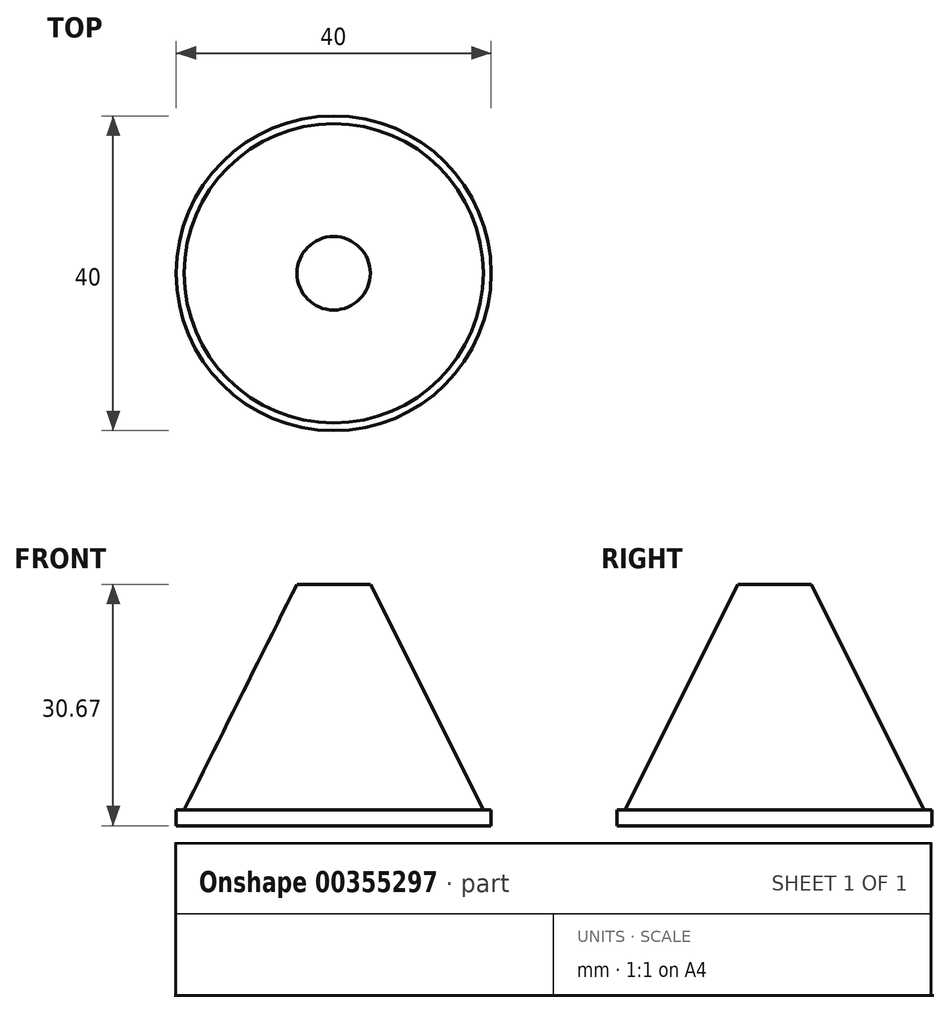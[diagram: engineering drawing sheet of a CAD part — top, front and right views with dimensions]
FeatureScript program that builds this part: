
annotation { "Feature Type Name" : "Feature", "Feature Type Description" : "" }
export const myFeature = defineFeature(function(context is Context, id is Id, definition is map)
    precondition{}
    {
        {
            var Q0;
            Q0=qCreatedBy(makeId("Front.planeOp"),FACE);
            var sketch = newSketch(context, id + "F0", { "sketchPlane" : qUnion([Q0])});
            skLineSegment(sketch, "E0", {"start": v(0, 0) * mm, "end": v(0, 40) * mm});
            skLineSegment(sketch, "E1", {"start": v(0, 40) * mm, "end": v(20, 0) * mm});
            skLineSegment(sketch, "E2", {"start": v(20, 0) * mm, "end": v(0, 0) * mm});
            skSolve(sketch);
        }
        {
            var Q0;
            Q0=makeQuery(id+"F0.imprint","IMPRINT",FACE,{"disambiguationData":[TD([[makeQuery(id+"F0.imprint","IMPRINT",EDGE,{"derivedFrom":sQuery(id+"F0.wireOp",EDGE,"E0")}),-1.0]])]});
            var Q1;
            Q1=sQuery(id+"F0.wireOp",EDGE,"E0");
            revolve(context, id + "F1", {"entities" : qUnion([Q0]), "axis" : qUnion([Q1]), "revolveType" : RevolveType.FULL});
        }
        {
            var Q0;
            Q0=qCreatedBy(makeId("Top.planeOp"),FACE);
            var sketch = newSketch(context, id + "F2", { "sketchPlane" : qUnion([Q0])});
            skCircle(sketch, "E3", {"center": v(0, 0) * mm, "radius": 20 * mm});
            skSolve(sketch);
        }
        {
            var Q0;
            Q0=makeQuery(id+"F2.imprint","IMPRINT",FACE,{"disambiguationData":[TD([[makeQuery(id+"F2.imprint","IMPRINT",EDGE,{"derivedFrom":sQuery(id+"F2.wireOp",EDGE,"E3")}),1.0]])]});
            extrude(context, id + "F3", {"entities" : qUnion([Q0]), "operationType" : NewBodyOperationType.ADD, "depth" : 2 * mm});
        }
        {
            var Q0;
            Q0=qCreatedBy(makeId("Front.planeOp"),FACE);
            var sketch = newSketch(context, id + "F4", { "sketchPlane" : qUnion([Q0])});
            skLineSegment(sketch, "E4.bottom", {"start": v(-7.07, 45.58) * mm, "end": v(8.07, 45.58) * mm});
            skLineSegment(sketch, "E4.top", {"start": v(-7.07, 30.67) * mm, "end": v(8.07, 30.67) * mm});
            skLineSegment(sketch, "E4.left", {"start": v(-7.07, 45.58) * mm, "end": v(-7.07, 30.67) * mm});
            skLineSegment(sketch, "E4.right", {"start": v(8.07, 45.58) * mm, "end": v(8.07, 30.67) * mm});
            skSolve(sketch);
        }
        {
            var Q0;
            Q0=makeQuery(id+"F4.imprint","IMPRINT",FACE,{"disambiguationData":[TD([[makeQuery(id+"F4.imprint","IMPRINT",EDGE,{"derivedFrom":sQuery(id+"F4.wireOp",EDGE,"E4.bottom")}),-1.0]])]});
            extrude(context, id + "F5", {"entities" : qUnion([Q0]), "operationType" : NewBodyOperationType.REMOVE, "oppositeDirection" : true, "depth" : 25 * mm, "hasSecondDirection" : true, "secondDirectionOppositeDirection" : false, "secondDirectionDepth" : 25 * mm});
        }
    });
